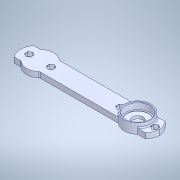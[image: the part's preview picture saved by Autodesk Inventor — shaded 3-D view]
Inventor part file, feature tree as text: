
AUTODESK INVENTOR PART (.ipt)
format: ipt  version: 2021 (Build 250183000, 183)  size: 362,496 bytes
history: native  units: in
note: dims shown in document units (in); Inventor stores cm internally (conversion verified against a paired STEP export)
features: sketch x14, extrude x11, fillet x2, projected_geometry x2, delete_face x1, chamfer x1, hole x1, other x1
ambient origin geometry x8: Origin, YZ Plane, XZ Plane, XY Plane, X Axis, Y Axis, Z Axis, Center Point
bodies: Solid1 (feature_tree)
feature tree (33):
  extrude  "Extrusion1"  Depth=0.3937in TaperAngle=0.0deg
  extrude  "Extrusion2"  TaperAngle=0.0deg  [1 undecoded]
  sketch  "Sketch5"  dims[d9=0.3937in d10=0.0in d11=0.878in d12=0.3937in d13=0.0in]
  delete_face  "Delete Face1"
  extrude  "Extrusion4"  Depth=0.3937in
  extrude  "Extrusion5"  Depth=0.3937in
  chamfer  "Chamfer1"  Distance=0.3937in
  sketch  "Sketch8"  dims[d32=0.3937in d33=0.0in d34=0.0787in d35=0.0787in d36=0.0in]
  extrude  "Extrusion7"  Depth=0.7087in
  extrude  "Extrusion9"  Depth=0.3937in
  extrude  "Extrusion8"  Depth=0.3937in
  fillet  "Fillet2"  Radius=0.0787in
  hole  "Hole1"  [1 undecoded]
  extrude  "Extrusion10"  Depth=0.2362in
  extrude  "Extrusion11"  Depth=1.1811in
  extrude  "Extrusion12"  Depth=0.3937in
  fillet  "Fillet3"  Radius=0.3937in
  extrude  "Extrusion3"  Depth=0.0118in
  sketch  "Sketch1"  dims[d0=0.7874in d1=0.3937in d2=0.0in]
  sketch  "Sketch2"  dims[d3=0.3937in d4=0.0in d5=0.0in]
  sketch  "Sketch4"  dims[d6=0.3937in d7=0.0in d8=0.9843in]
  sketch  "Sketch6"  dims[d14=0.0197in d15=0.0787in d16=45.0deg d28=0.7087in]
  sketch  "Sketch7"  dims[d29=0.3937in d30=0.0in d31=3.5433in]
  sketch  "Sketch11"  dims[d37=0.7874in d39=0.4921in]
  sketch  "Sketch12"  dims[d40=0.1378in d41=0.2362in d42=0.1575in d43=0.0787in d44=90.0deg d45=0.315in d46=0.8108in d47=0.2264in]
  sketch  "Sketch13"  dims[d48=0.0787in d49=0.0in d50=1.1811in]
  sketch  "Sketch14"  dims[d52=0.1181in d53=0.1378in d54=0.3937in d55=0.0in]
  projected_geometry  "Projected Loop3"
  projected_geometry  "Projected Loop4"
  sketch  "Sketch15"  dims[d56=0.0472in d57=0.0118in]
  sketch  "Sketch16"  dims[d60=0.0591in d61=0.0in]
  sketch  "Sketch17"  dims[d62=0.0394in]
  other  "Cut-Extrude3"
note: 2 required parameter values undecoded (feature->parameter linkage not recoverable at this tier; creation-order binding heuristic only, values carry confidence <= 0.55)
